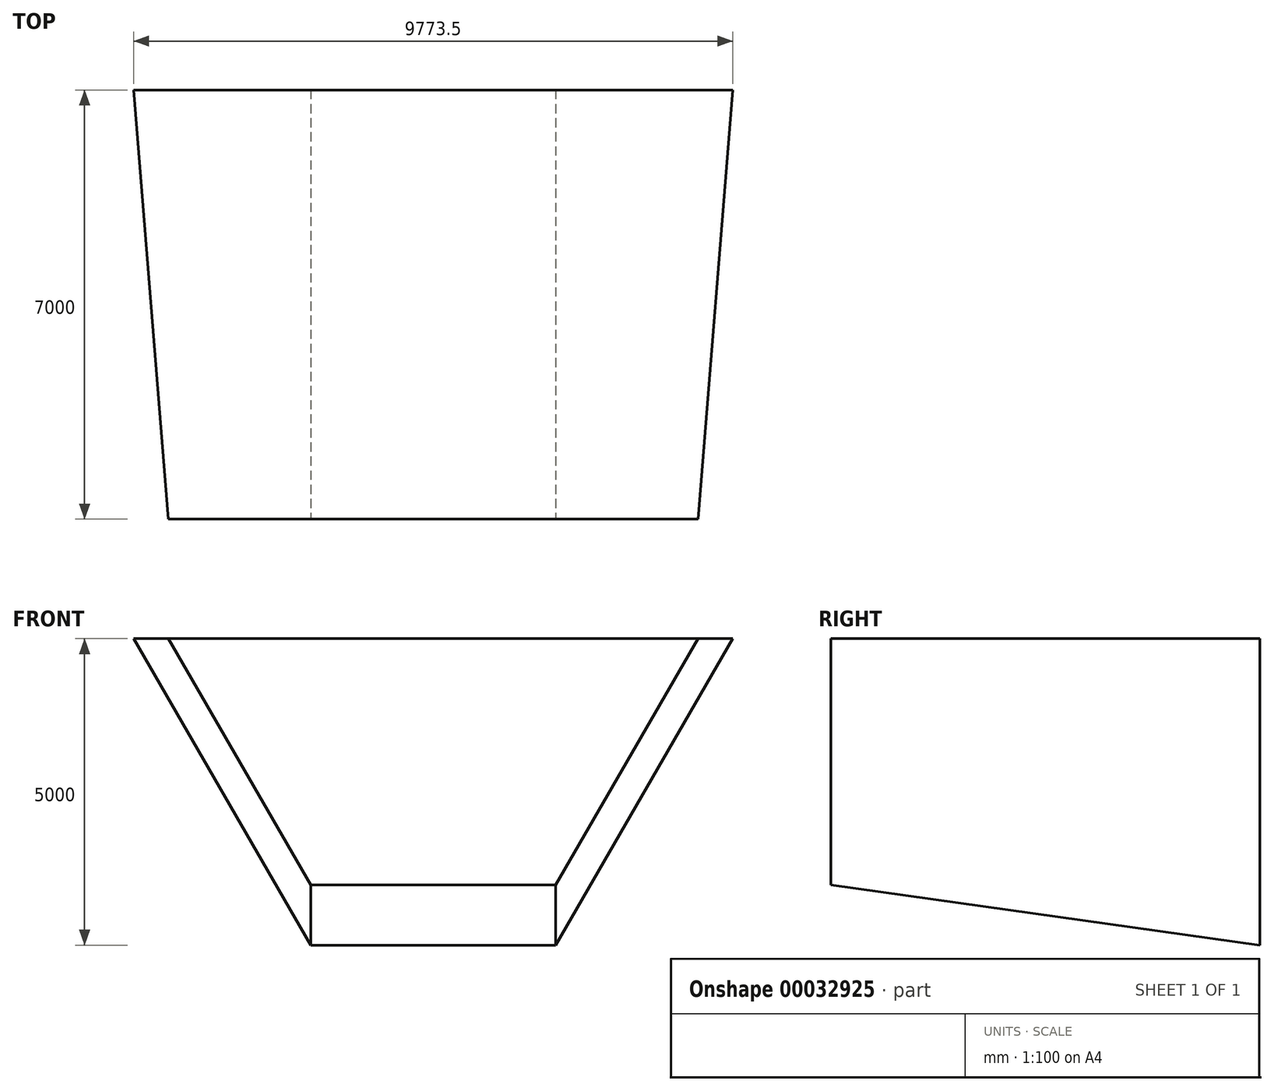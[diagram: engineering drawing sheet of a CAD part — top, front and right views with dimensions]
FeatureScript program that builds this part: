
annotation { "Feature Type Name" : "Feature", "Feature Type Description" : "" }
export const myFeature = defineFeature(function(context is Context, id is Id, definition is map)
    precondition{}
    {
        {
            var Q0;
            Q0=qCreatedBy(makeId("Front.planeOp"),FACE);
            var sketch = newSketch(context, id + "F0", { "sketchPlane" : qUnion([Q0])});
            skLineSegment(sketch, "E0", {"start": v(-2000, 0) * mm, "end": v(2000, 0) * mm});
            skLineSegment(sketch, "E1", {"start": v(2000, 0) * mm, "end": v(4886.75, 5000) * mm});
            skLineSegment(sketch, "E2", {"start": v(4886.75, 5000) * mm, "end": v(-4886.75, 5000) * mm});
            skLineSegment(sketch, "E3", {"start": v(-4886.75, 5000) * mm, "end": v(-2000, 0) * mm});
            skSolve(sketch);
        }
        {
            var Q0;
            Q0=qCreatedBy(makeId("Right.planeOp"),FACE);
            var sketch = newSketch(context, id + "F1", { "sketchPlane" : qUnion([Q0])});
            skLineSegment(sketch, "E4", {"start": v(0, 0) * mm, "end": v(-7000, 983.79) * mm});
            skLineSegment(sketch, "E5", {"start": v(-7000, 983.79) * mm, "end": v(-7000, 5000) * mm});
            skLineSegment(sketch, "E6", {"start": v(-7000, 5000) * mm, "end": v(0, 5000) * mm});
            skLineSegment(sketch, "E7", {"start": v(0, 0) * mm, "end": v(-9047.36, 0) * mm, "construction": true});
            skSolve(sketch);
        }
        {
            var Q0;
            Q0=sQuery(id+"F1.wireOp",VERTEX,"E6.start");
            var Q1;
            Q1=sQuery(id+"F1.wireOp",EDGE,"E6");
            cPlane(context, id + "F2", {"entities" : qUnion([Q0, Q1]), "cplaneType" : CPlaneType.LINE_POINT, "offset" : 6000 * mm, "width" : 152.4 * mm, "height" : 152.4 * mm});
        }
        {
            var Q0;
            Q0=qCreatedBy(id+"F2.planeOp",FACE);
            var sketch = newSketch(context, id + "F3", { "sketchPlane" : qUnion([Q0])});
            skLineSegment(sketch, "E8", {"start": v(-4318.76, 5000) * mm, "end": v(4318.76, 5000) * mm});
            skLineSegment(sketch, "E9", {"start": v(2000, 983.79) * mm, "end": v(-2000, 983.79) * mm});
            skLineSegment(sketch, "E10", {"start": v(-2000, 983.79) * mm, "end": v(-4318.76, 5000) * mm});
            skLineSegment(sketch, "E11", {"start": v(2000, 983.79) * mm, "end": v(4318.76, 5000) * mm});
            skSolve(sketch);
        }
        {
            var Q0;
            Q0=makeQuery(id+"F0.imprint","IMPRINT",FACE,{"disambiguationData":[TD([[makeQuery(id+"F0.imprint","IMPRINT",EDGE,{"derivedFrom":sQuery(id+"F0.wireOp",EDGE,"E0")}),1.0]])]});
            var Q1;
            Q1=makeQuery(id+"F3.imprint","IMPRINT",FACE,{"disambiguationData":[TD([[makeQuery(id+"F3.imprint","IMPRINT",EDGE,{"derivedFrom":sQuery(id+"F3.wireOp",EDGE,"E8")}),-1.0]])]});
            loft(context, id + "F4", {"sheetProfilesArray" : [{ "sheetProfileEntities" : qUnion([Q0]) }, { "sheetProfileEntities" : qUnion([Q1]) }]});
        }
    });
